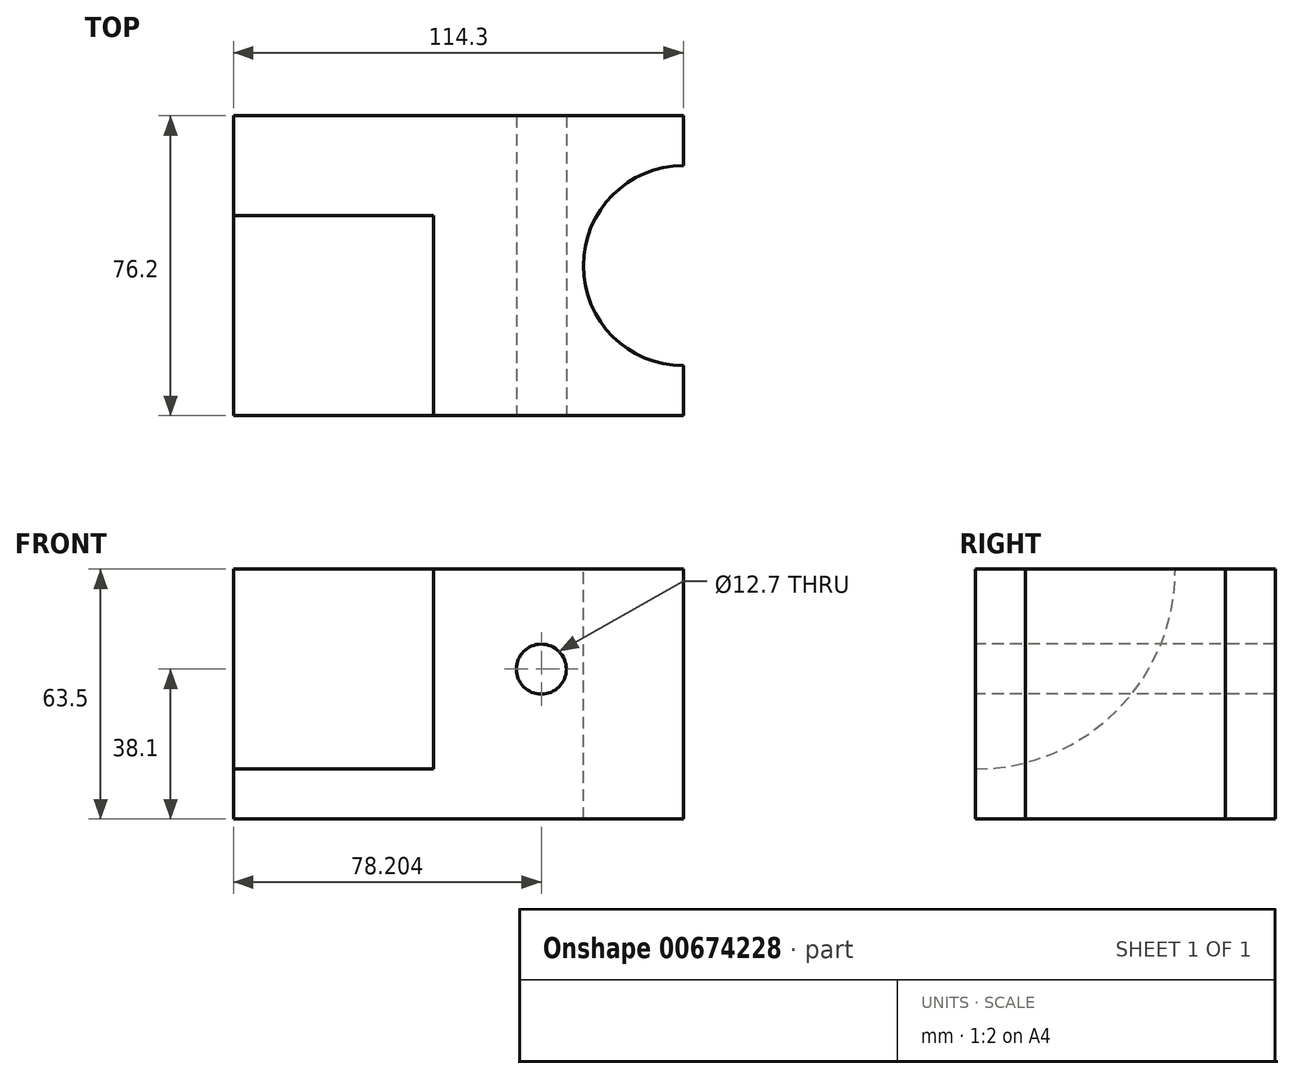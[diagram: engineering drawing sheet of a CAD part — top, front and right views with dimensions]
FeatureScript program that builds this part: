
annotation { "Feature Type Name" : "Feature", "Feature Type Description" : "" }
export const myFeature = defineFeature(function(context is Context, id is Id, definition is map)
    precondition{}
    {
        {
            var Q0;
            Q0=qCreatedBy(makeId("Front.planeOp"),FACE);
            var sketch = newSketch(context, id + "F0", { "sketchPlane" : qUnion([Q0])});
            skLineSegment(sketch, "E0.bottom", {"start": v(57.15, -31.75) * mm, "end": v(-57.15, -31.75) * mm});
            skLineSegment(sketch, "E0.top", {"start": v(57.15, 31.75) * mm, "end": v(-57.15, 31.75) * mm});
            skLineSegment(sketch, "E0.left", {"start": v(57.15, -31.75) * mm, "end": v(57.15, 31.75) * mm});
            skLineSegment(sketch, "E0.right", {"start": v(-57.15, -31.75) * mm, "end": v(-57.15, 31.75) * mm});
            skPoint(sketch, "E0.middle", {"position": v(0, 0) * mm});
            skSolve(sketch);
        }
        {
            var Q0;
            Q0 = qSketchRegion(id + "F0", true);
            extrude(context, id + "F1", {"entities" : qUnion([Q0]), "depth" : 76.2 * mm, "offsetDistance" : 25.4 * mm});
        }
        {
            var Q0;
            Q0=makeQuery(id+"F1.opExtrude","SWEPT_FACE",FACE,{"disambiguationData":[OSD([sQuery(id+"F0.wireOp",EDGE,"E0.right")])]});
            var sketch = newSketch(context, id + "F2", { "sketchPlane" : qUnion([Q0])});
            skCircle(sketch, "E1", {"center": v(76.2, 31.75) * mm, "radius": 50.8 * mm});
            skSolve(sketch);
        }
        {
            var Q0;
            Q0 = qSketchRegion(id + "F2", true);
            extrude(context, id + "F3", {"entities" : qUnion([Q0]), "operationType" : NewBodyOperationType.REMOVE, "oppositeDirection" : true, "depth" : 50.8 * mm, "offsetDistance" : 25.4 * mm});
        }
        {
            var Q0;
            Q0=makeQuery(id+"F1.opExtrude","CAP_FACE",FACE,{"disambiguationData":[OSD([sQuery(id+"F0.wireOp",EDGE,"E0.bottom"),sQuery(id+"F0.wireOp",EDGE,"E0.top"),sQuery(id+"F0.wireOp",EDGE,"E0.left"),sQuery(id+"F0.wireOp",EDGE,"E0.right")])],"isStart":false});
            var sketch = newSketch(context, id + "F4", { "sketchPlane" : qUnion([Q0])});
            skCircle(sketch, "E2", {"center": v(21.05, 6.35) * mm, "radius": 6.35 * mm});
            skSolve(sketch);
        }
        {
            var Q0;
            Q0 = qSketchRegion(id + "F4", true);
            extrude(context, id + "F5", {"entities" : qUnion([Q0]), "operationType" : NewBodyOperationType.REMOVE, "oppositeDirection" : true, "depth" : 76.2 * mm, "offsetDistance" : 25.4 * mm});
        }
        {
            var Q0;
            Q0=makeQuery(id+"F1.opExtrude","SWEPT_FACE",FACE,{"disambiguationData":[OSD([sQuery(id+"F0.wireOp",EDGE,"E0.top")])]});
            var sketch = newSketch(context, id + "F6", { "sketchPlane" : qUnion([Q0])});
            skCircle(sketch, "E3", {"center": v(57.15, -38.1) * mm, "radius": 25.4 * mm});
            skSolve(sketch);
        }
        {
            var Q0;
            Q0 = qSketchRegion(id + "F6", true);
            extrude(context, id + "F7", {"entities" : qUnion([Q0]), "operationType" : NewBodyOperationType.REMOVE, "oppositeDirection" : true, "depth" : 87.38 * mm, "offsetDistance" : 25.4 * mm});
        }
    });
